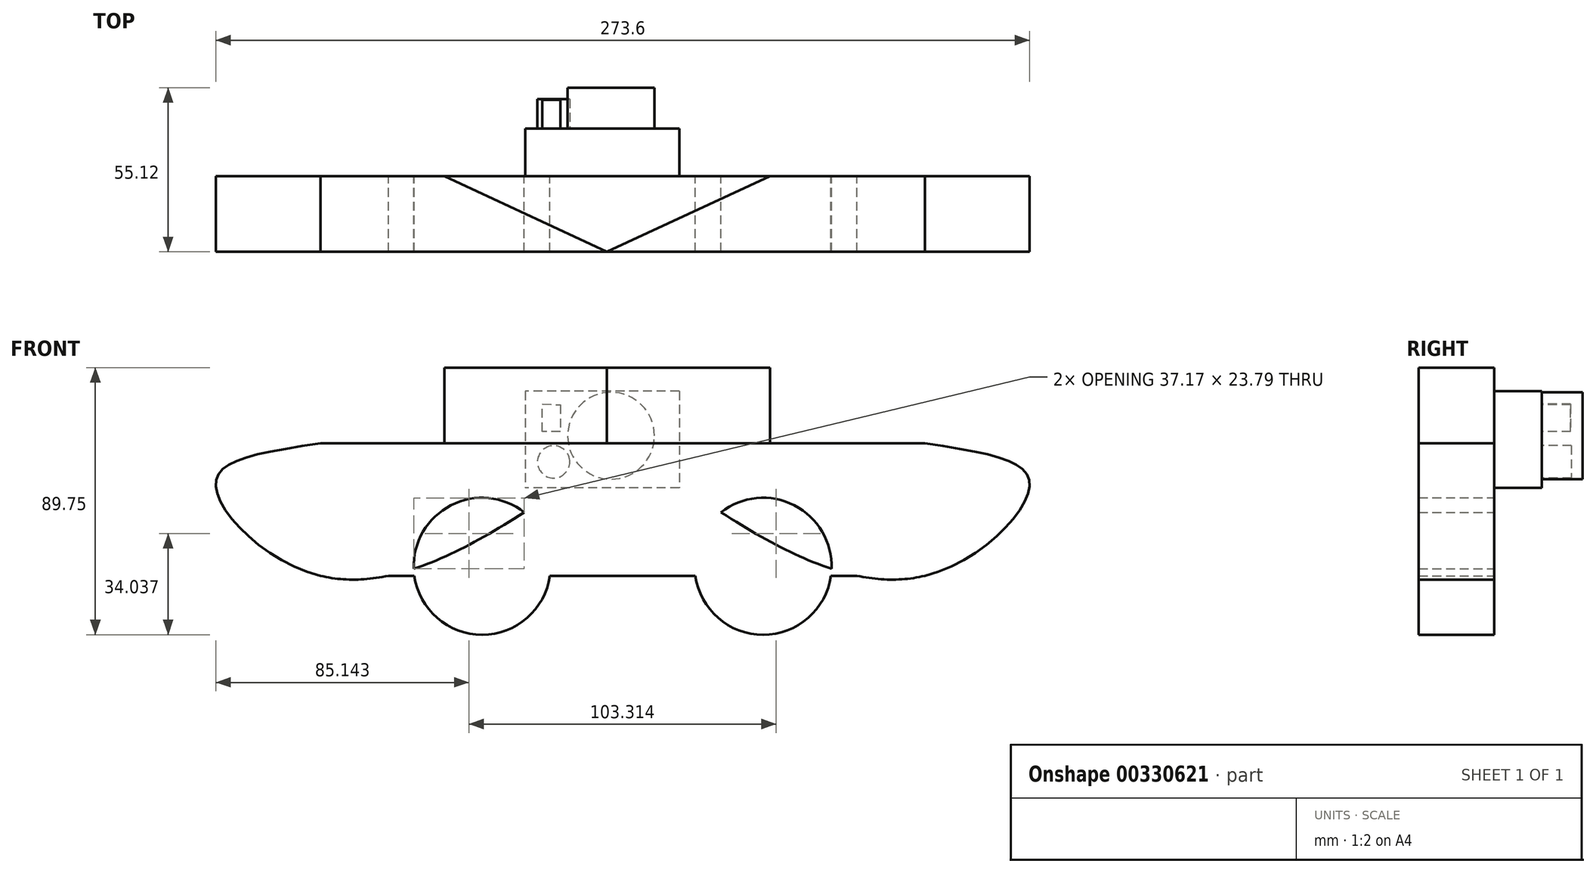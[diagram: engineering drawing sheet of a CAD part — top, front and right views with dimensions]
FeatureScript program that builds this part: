
annotation { "Feature Type Name" : "Feature", "Feature Type Description" : "" }
export const myFeature = defineFeature(function(context is Context, id is Id, definition is map)
    precondition{}
    {
        {
            var Q0;
            Q0=qCreatedBy(makeId("Front.planeOp"),FACE);
            var sketch = newSketch(context, id + "F0", { "sketchPlane" : qUnion([Q0])});
            skLineSegment(sketch, "E0.bottom", {"start": v(0, 0) * mm, "end": v(-101.6, 0) * mm});
            skLineSegment(sketch, "E0.top", {"start": v(0, 44.52) * mm, "end": v(-101.6, 44.52) * mm});
            skLineSegment(sketch, "E0.left", {"start": v(0, 0) * mm, "end": v(0, 44.52) * mm});
            skLineSegment(sketch, "E0.right", {"start": v(-101.6, 0) * mm, "end": v(-101.6, 44.52) * mm});
            skCircle(sketch, "E1", {"center": v(-54.36, 3.19) * mm, "radius": 23.02 * mm});
            skFitSpline(sketch, "E2", {"points": [v(0, 44.52) * mm, v(35.18, 30.27) * mm, v(0, 0) * mm, v(-101.6, 44.52) * mm], "startDerivative": vector(266.93, -39.84) * mm, "endDerivative": vector(-269.48, 198.48) * mm});
            skFitSpline(sketch, "E3.MirrorCS", {"points": [v(-203.2, 44.52) * mm, v(-238.38, 30.27) * mm, v(-203.2, 0) * mm, v(-101.6, 44.52) * mm], "startDerivative": vector(-266.93, -39.84) * mm, "endDerivative": vector(269.48, 198.48) * mm});
            skFitSpline(sketch, "E4.MirrorCS", {"points": [v(-203.2, 44.52) * mm, v(-238.38, 30.27) * mm, v(-203.2, 0) * mm, v(-101.6, 44.52) * mm], "startDerivative": vector(-266.93, -39.84) * mm, "endDerivative": vector(269.48, 198.48) * mm});
            skLineSegment(sketch, "E5.MirrorCS", {"start": v(-203.2, 44.52) * mm, "end": v(-101.6, 44.52) * mm});
            skCircle(sketch, "E6.MirrorC", {"center": v(-148.84, 3.19) * mm, "radius": 23.02 * mm});
            skLineSegment(sketch, "E7.MirrorCS", {"start": v(-203.2, 0) * mm, "end": v(-101.6, 0) * mm});
            skSolve(sketch);
        }
        {
            var Q0;
            Q0 = qSketchRegion(id + "F0", true);
            extrude(context, id + "F1", {"entities" : qUnion([Q0]), "depth" : 25.4 * mm});
        }
        {
            var Q0;
            Q0=makeQuery(id+"F1.opExtrude","SWEPT_FACE",FACE,{"disambiguationData":[OSD([sQuery(id+"F0.wireOp",EDGE,"E0.top"),sQuery(id+"F0.wireOp",EDGE,"E5.MirrorCS")])]});
            var sketch = newSketch(context, id + "F2", { "sketchPlane" : qUnion([Q0])});
            skLineSegment(sketch, "E8", {"start": v(-106.83, 0) * mm, "end": v(-106.83, -25.4) * mm});
            skLineSegment(sketch, "E9", {"start": v(-106.83, -25.4) * mm, "end": v(-161.56, 0) * mm});
            skLineSegment(sketch, "E10", {"start": v(-106.83, -25.4) * mm, "end": v(-52.1, 0) * mm});
            skSolve(sketch);
        }
        {
            var Q0;
            {var subQ0=sQuery(id+"F2.wireOp",EDGE,"E8");Q0=makeQuery(id+"F2.imprint","IMPRINT",FACE,{"disambiguationData":[TD([[makeQuery(id+"F2.imprint","IMPRINT",EDGE,{"derivedFrom":subQ0}),-1.0]])]});}
            var Q1;
            {var subQ0=sQuery(id+"F2.wireOp",EDGE,"E8");Q1=makeQuery(id+"F2.imprint","IMPRINT",FACE,{"disambiguationData":[TD([[makeQuery(id+"F2.imprint","IMPRINT",EDGE,{"derivedFrom":subQ0}),1.0]])]});}
            extrude(context, id + "F3", {"entities" : qUnion([Q0, Q1]), "operationType" : NewBodyOperationType.ADD, "depth" : 25.4 * mm});
        }
        {
            var Q0;
            {var subQ0=sQuery(id+"F0.wireOp",EDGE,"E5.MirrorCS");var subQ1=sQuery(id+"F0.wireOp",EDGE,"E0.top");Q0=makeQuery(id+"F3.boolean.opBoolean","MERGE",FACE,{"derivedFrom":[makeQuery(id+"F1.opExtrude","CAP_FACE",FACE,{"disambiguationData":[OSD([sQuery(id+"F0.wireOp",EDGE,"E0.bottom"),subQ1,sQuery(id+"F0.wireOp",EDGE,"E1"),sQuery(id+"F0.wireOp",EDGE,"E2"),sQuery(id+"F0.wireOp",EDGE,"E4.MirrorCS"),subQ0,sQuery(id+"F0.wireOp",EDGE,"E6.MirrorC"),sQuery(id+"F0.wireOp",EDGE,"E7.MirrorCS")])],"isStart":true}),makeQuery(id+"F3.opExtrude","SWEPT_FACE",FACE,{"disambiguationData":[OSD([subQ1,subQ0])]})]});}
            var sketch = newSketch(context, id + "F4", { "sketchPlane" : qUnion([Q0])});
            skLineSegment(sketch, "E11.bottom", {"start": v(82.44, 61.65) * mm, "end": v(128.72, 61.65) * mm});
            skLineSegment(sketch, "E11.top", {"start": v(82.44, 32.07) * mm, "end": v(128.72, 32.07) * mm});
            skLineSegment(sketch, "E11.left", {"start": v(82.44, 61.65) * mm, "end": v(82.44, 32.07) * mm});
            skLineSegment(sketch, "E11.right", {"start": v(128.72, 61.65) * mm, "end": v(128.72, 32.07) * mm});
            skCircle(sketch, "E12", {"center": v(105.49, 47.05) * mm, "radius": 14.6 * mm});
            skLineSegment(sketch, "E13", {"start": v(128.72, 32.07) * mm, "end": v(128.72, 61.65) * mm});
            skSolve(sketch);
        }
        {
            var Q0;
            Q0=makeQuery(id+"F4.imprint","IMPRINT",FACE,{"disambiguationData":[TD([[makeQuery(id+"F4.imprint","IMPRINT",EDGE,{"derivedFrom":sQuery(id+"F4.wireOp",EDGE,"E12")}),1.0]])]});
            extrude(context, id + "F5", {"entities" : qUnion([Q0]), "operationType" : NewBodyOperationType.ADD, "depth" : 29.72 * mm});
        }
        {
            var Q0;
            {var subQ0=sQuery(id+"F0.wireOp",EDGE,"E5.MirrorCS");var subQ1=sQuery(id+"F0.wireOp",EDGE,"E0.top");Q0=makeQuery(id+"F3.boolean.opBoolean","MERGE",FACE,{"derivedFrom":[makeQuery(id+"F1.opExtrude","CAP_FACE",FACE,{"disambiguationData":[OSD([sQuery(id+"F0.wireOp",EDGE,"E0.bottom"),subQ1,sQuery(id+"F0.wireOp",EDGE,"E1"),sQuery(id+"F0.wireOp",EDGE,"E2"),sQuery(id+"F0.wireOp",EDGE,"E4.MirrorCS"),subQ0,sQuery(id+"F0.wireOp",EDGE,"E6.MirrorC"),sQuery(id+"F0.wireOp",EDGE,"E7.MirrorCS")])],"isStart":true}),makeQuery(id+"F3.opExtrude","SWEPT_FACE",FACE,{"disambiguationData":[OSD([subQ1,subQ0])]})]});}
            var sketch = newSketch(context, id + "F6", { "sketchPlane" : qUnion([Q0])});
            skLineSegment(sketch, "E14.bottom", {"start": v(82.55, 62.05) * mm, "end": v(134.3, 62.05) * mm});
            skLineSegment(sketch, "E14.top", {"start": v(82.55, 29.6) * mm, "end": v(134.3, 29.6) * mm});
            skLineSegment(sketch, "E14.left", {"start": v(82.55, 62.05) * mm, "end": v(82.55, 29.6) * mm});
            skLineSegment(sketch, "E14.right", {"start": v(134.3, 62.05) * mm, "end": v(134.3, 29.6) * mm});
            skSolve(sketch);
        }
        {
            var Q0;
            Q0 = qSketchRegion(id + "F6", true);
            extrude(context, id + "F7", {"entities" : qUnion([Q0]), "operationType" : NewBodyOperationType.ADD, "depth" : 16 * mm});
        }
        {
            var Q0;
            Q0=makeQuery(id+"F7.opExtrude","CAP_FACE",FACE,{"disambiguationData":[OSD([sQuery(id+"F6.wireOp",EDGE,"E14.bottom"),sQuery(id+"F6.wireOp",EDGE,"E14.top"),sQuery(id+"F6.wireOp",EDGE,"E14.left"),sQuery(id+"F6.wireOp",EDGE,"E14.right")])],"isStart":false});
            var sketch = newSketch(context, id + "F8", { "sketchPlane" : qUnion([Q0])});
            skLineSegment(sketch, "E15", {"start": v(122.54, 57.42) * mm, "end": v(122.54, 48.5) * mm});
            skLineSegment(sketch, "E16", {"start": v(122.54, 48.5) * mm, "end": v(128.58, 48.5) * mm});
            skLineSegment(sketch, "E17", {"start": v(128.58, 48.5) * mm, "end": v(128.58, 57.74) * mm});
            skLineSegment(sketch, "E18", {"start": v(128.58, 57.74) * mm, "end": v(122.54, 57.42) * mm});
            skCircle(sketch, "E19", {"center": v(124.8, 38.27) * mm, "radius": 5.44 * mm});
            skSolve(sketch);
        }
        {
            var Q0;
            Q0=makeQuery(id+"F8.imprint","IMPRINT",FACE,{"disambiguationData":[TD([[makeQuery(id+"F8.imprint","IMPRINT",EDGE,{"derivedFrom":sQuery(id+"F8.wireOp",EDGE,"E15")}),1.0]])]});
            extrude(context, id + "F9", {"entities" : qUnion([Q0]), "operationType" : NewBodyOperationType.ADD, "depth" : 9.65 * mm});
        }
        {
            var Q0;
            Q0=makeQuery(id+"F8.imprint","IMPRINT",FACE,{"disambiguationData":[TD([[makeQuery(id+"F8.imprint","IMPRINT",EDGE,{"derivedFrom":sQuery(id+"F8.wireOp",EDGE,"E19")}),1.0]])]});
            extrude(context, id + "F10", {"entities" : qUnion([Q0]), "operationType" : NewBodyOperationType.ADD, "depth" : 9.9 * mm});
        }
    });
